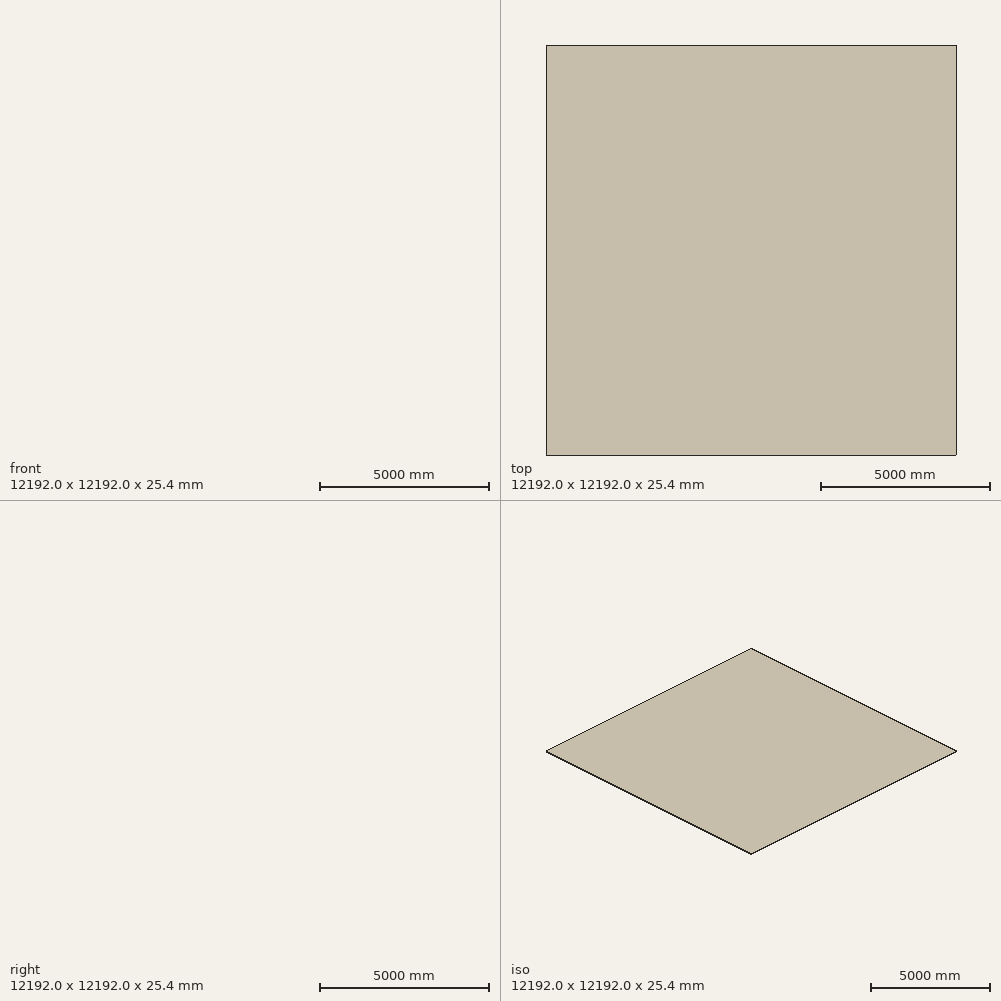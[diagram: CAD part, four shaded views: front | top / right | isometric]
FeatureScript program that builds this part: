
annotation { "Feature Type Name" : "Feature", "Feature Type Description" : "" }
export const myFeature = defineFeature(function(context is Context, id is Id, definition is map)
    precondition{}
    {
        {
            var Q0;
            Q0=qCreatedBy(makeId("Top.planeOp"),FACE);
            var sketch = newSketch(context, id + "F0", { "sketchPlane" : qUnion([Q0])});
            skLineSegment(sketch, "E0.bottom", {"start": v(0, 0) * mm, "end": v(-12192, 0) * mm});
            skLineSegment(sketch, "E0.top", {"start": v(0, -12192) * mm, "end": v(-12192, -12192) * mm});
            skLineSegment(sketch, "E0.left", {"start": v(0, 0) * mm, "end": v(0, -12192) * mm});
            skLineSegment(sketch, "E0.right", {"start": v(-12192, 0) * mm, "end": v(-12192, -12192) * mm});
            skSolve(sketch);
        }
        {
            var Q0;
            Q0 = qSketchRegion(id + "F0", true);
            extrude(context, id + "F1", {"entities" : qUnion([Q0]), "depth" : 25.4 * mm, "offsetDistance" : 25.4 * mm});
        }
    });
